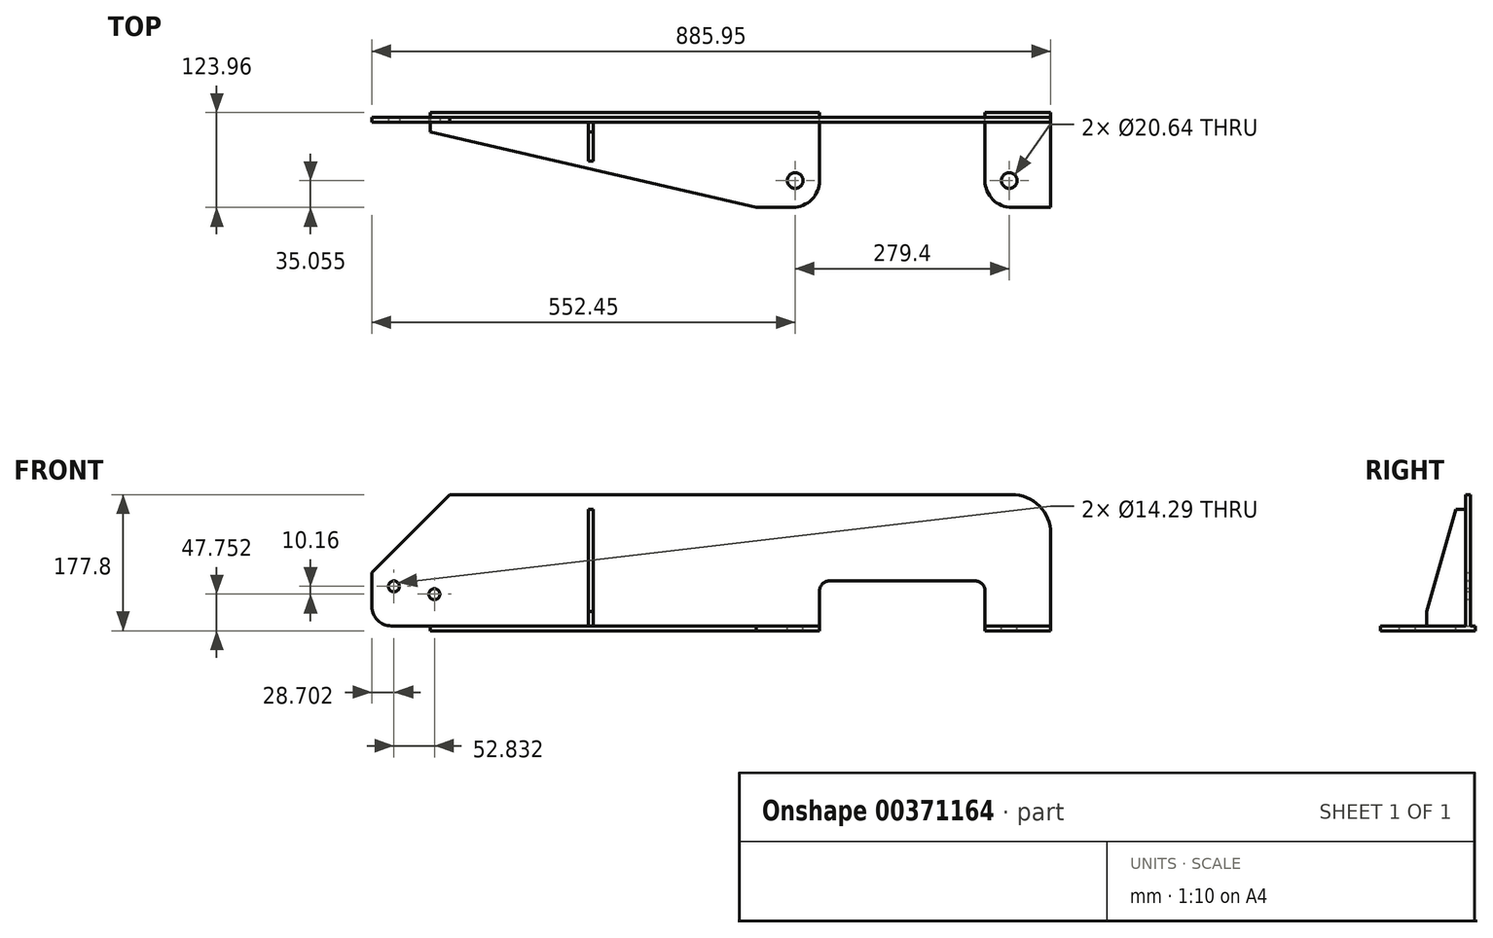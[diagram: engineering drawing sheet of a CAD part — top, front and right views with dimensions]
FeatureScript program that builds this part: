
annotation { "Feature Type Name" : "Feature", "Feature Type Description" : "" }
export const myFeature = defineFeature(function(context is Context, id is Id, definition is map)
    precondition{}
    {
        {
            var Q0;
            Q0=qCreatedBy(makeId("Front.planeOp"),FACE);
            var sketch = newSketch(context, id + "F0", { "sketchPlane" : qUnion([Q0])});
            skLineSegment(sketch, "E0", {"start": v(0, 99.97) * mm, "end": v(0, -95.52) * mm, "construction": true});
            skLineSegment(sketch, "E1.0", {"start": v(-107.95, 99.97) * mm, "end": v(-107.95, -95.52) * mm, "construction": true});
            skLineSegment(sketch, "E2.MirrorCS", {"start": v(107.95, 99.97) * mm, "end": v(107.95, -95.52) * mm, "construction": true});
            skLineSegment(sketch, "E3", {"start": v(-692.15, 0) * mm, "end": v(137.63, 0) * mm, "construction": true});
            skLineSegment(sketch, "E4.0", {"start": v(-198.58, 58.67) * mm, "end": v(137.63, 58.67) * mm, "construction": true});
            skLineSegment(sketch, "E5.0", {"start": v(-198.58, 171.45) * mm, "end": v(137.63, 171.45) * mm, "construction": true});
            skLineSegment(sketch, "E6.0", {"start": v(193.8, 171.45) * mm, "end": v(193.8, -95.52) * mm, "construction": true});
            skLineSegment(sketch, "E7.0", {"start": v(-692.15, 99.97) * mm, "end": v(-692.15, -95.52) * mm, "construction": true});
            skPoint(sketch, "E8.orphan", {"position": v(-198.58, 0) * mm});
            skLineSegment(sketch, "E9.bottom", {"start": v(-692.15, 0) * mm, "end": v(0, 0) * mm});
            skLineSegment(sketch, "E9.top", {"start": v(-692.15, 171.45) * mm, "end": v(143, 171.45) * mm});
            skLineSegment(sketch, "E9.left", {"start": v(-692.15, 0) * mm, "end": v(-692.15, 171.45) * mm});
            skLineSegment(sketch, "E9.right", {"start": v(193.8, 0) * mm, "end": v(193.8, 120.65) * mm});
            skLineSegment(sketch, "E10.bottom", {"start": v(-95.25, 58.67) * mm, "end": v(95.25, 58.67) * mm});
            skLineSegment(sketch, "E10.top", {"start": v(-107.95, 0) * mm, "end": v(0, 0) * mm});
            skLineSegment(sketch, "E10.left", {"start": v(-107.95, 45.97) * mm, "end": v(-107.95, 0) * mm});
            skLineSegment(sketch, "E10.right", {"start": v(107.95, 45.97) * mm, "end": v(107.95, 0) * mm});
            skLineSegment(sketch, "E11.trimOffspring", {"start": v(107.95, 0) * mm, "end": v(193.8, 0) * mm});
            skPoint(sketch, "E12.visualSharp", {"position": v(-107.95, 58.67) * mm});
            skArc(sketch, "E12.filletArc", {"start": v(-95.25, 58.67) * mm, "mid": v(-104.23, 54.95) * mm, "end": v(-107.95, 45.97) * mm});
            skPoint(sketch, "E13.visualSharp", {"position": v(107.95, 58.67) * mm});
            skArc(sketch, "E13.filletArc", {"start": v(107.95, 45.97) * mm, "mid": v(104.23, 54.95) * mm, "end": v(95.25, 58.67) * mm});
            skPoint(sketch, "E14.visualSharp", {"position": v(193.8, 171.45) * mm});
            skArc(sketch, "E14.filletArc", {"start": v(193.8, 120.65) * mm, "mid": v(178.92, 156.57) * mm, "end": v(143, 171.45) * mm});
            skSolve(sketch);
        }
        {
            var Q0;
            Q0 = qSketchRegion(id + "F0", true);
            extrude(context, id + "F1", {"entities" : qUnion([Q0]), "endBound" : BoundingType.SYMMETRIC, "depth" : 6.35 * mm});
        }
        {
            var Q0;
            Q0=makeQuery(id+"F1.opExtrude","SWEPT_EDGE",EDGE,{"disambiguationData":[OSD([sQuery(id+"F0.wireOp",EDGE,"E9.top"),sQuery(id+"F0.wireOp",EDGE,"E9.left")])]});
            chamfer(context, id + "F2", {"entities" : qUnion([Q0]), "width" : 101.6 * mm, "tangentPropagation" : true});
        }
        {
            var Q0;
            Q0=makeQuery(id+"F1.opExtrude","CAP_FACE",FACE,{"disambiguationData":[OSD([sQuery(id+"F0.wireOp",EDGE,"E9.bottom"),sQuery(id+"F0.wireOp",EDGE,"E9.top"),sQuery(id+"F0.wireOp",EDGE,"E9.left"),sQuery(id+"F0.wireOp",EDGE,"E9.right"),sQuery(id+"F0.wireOp",EDGE,"E10.bottom"),sQuery(id+"F0.wireOp",EDGE,"E10.left"),sQuery(id+"F0.wireOp",EDGE,"E10.right"),sQuery(id+"F0.wireOp",EDGE,"E11.trimOffspring"),sQuery(id+"F0.wireOp",EDGE,"E12.filletArc"),sQuery(id+"F0.wireOp",EDGE,"E13.filletArc"),sQuery(id+"F0.wireOp",EDGE,"E14.filletArc")])],"isStart":false});
            var sketch = newSketch(context, id + "F3", { "sketchPlane" : qUnion([Q0])});
            skLineSegment(sketch, "E15.0", {"start": v(-692.15, 0) * mm, "end": v(-692.15, 69.85) * mm, "construction": true});
            skLineSegment(sketch, "E16.0", {"start": v(-692.15, 0) * mm, "end": v(-107.95, 0) * mm, "construction": true});
            skLineSegment(sketch, "E17.0", {"start": v(-610.62, 0) * mm, "end": v(-610.62, 44.45) * mm, "construction": true});
            skLineSegment(sketch, "E18.0", {"start": v(-692.15, 41.4) * mm, "end": v(-107.95, 41.4) * mm, "construction": true});
            skPoint(sketch, "E19", {"position": v(-610.62, 41.4) * mm});
            skLineSegment(sketch, "E20.0", {"start": v(-663.45, 0) * mm, "end": v(-663.45, 51.56) * mm, "construction": true});
            skLineSegment(sketch, "E21.0", {"start": v(-692.15, 51.56) * mm, "end": v(-107.95, 51.56) * mm, "construction": true});
            skPoint(sketch, "E22", {"position": v(-663.45, 51.56) * mm});
            skSolve(sketch);
        }
        {
            var Q0;
            Q0=sQuery(id+"F3.wireOp",VERTEX,"E19");
            var Q1;
            Q1=sQuery(id+"F3.wireOp",VERTEX,"E22");
            var Q2;
            Q2=makeQuery(id+"F1.opExtrude","SWEPT_BODY",BODY,{"disambiguationData":[OSD([sQuery(id+"F0.wireOp",EDGE,"E9.bottom"),sQuery(id+"F0.wireOp",EDGE,"E9.top"),sQuery(id+"F0.wireOp",EDGE,"E9.left"),sQuery(id+"F0.wireOp",EDGE,"E9.right"),sQuery(id+"F0.wireOp",EDGE,"E10.bottom"),sQuery(id+"F0.wireOp",EDGE,"E10.left"),sQuery(id+"F0.wireOp",EDGE,"E10.right"),sQuery(id+"F0.wireOp",EDGE,"E11.trimOffspring"),sQuery(id+"F0.wireOp",EDGE,"E12.filletArc"),sQuery(id+"F0.wireOp",EDGE,"E13.filletArc"),sQuery(id+"F0.wireOp",EDGE,"E14.filletArc")])]});
            hole(context, id + "F4", {"style" : HoleStyle.SIMPLE, "endStyle" : HoleEndStyle.THROUGH, "holeDiameter" : 14.29 * mm, "isTappedThrough" : true, "tappedDepth" : 7.75 * mm, "tapClearance" : 3, "locations" : qUnion([Q0, Q1]), "scope" : qUnion([Q2])});
        }
        {
            var Q0;
            Q0=qCreatedBy(makeId("Top.planeOp"),FACE);
            var sketch = newSketch(context, id + "F5", { "sketchPlane" : qUnion([Q0])});
            skLineSegment(sketch, "E23.0", {"start": v(-615.94, 9.53) * mm, "end": v(193.8, 9.53) * mm});
            skLineSegment(sketch, "E24.0", {"start": v(-565.15, -114.43) * mm, "end": v(-143, -114.43) * mm});
            skLineSegment(sketch, "E25.0", {"start": v(193.8, -114.43) * mm, "end": v(193.8, 9.53) * mm});
            skPoint(sketch, "E26.orphan", {"position": v(193.8, 3.17) * mm});
            skLineSegment(sketch, "E27.0", {"start": v(107.95, -79.38) * mm, "end": v(107.95, 9.53) * mm});
            skLineSegment(sketch, "E28.0", {"start": v(-107.95, -79.38) * mm, "end": v(-107.95, 9.53) * mm});
            skPoint(sketch, "E29.orphan", {"position": v(193.8, -3.18) * mm});
            skLineSegment(sketch, "E30.trimOffspring", {"start": v(143, -114.43) * mm, "end": v(193.8, -114.43) * mm});
            skPoint(sketch, "E31.visualSharp", {"position": v(107.95, -114.43) * mm});
            skArc(sketch, "E31.filletArc", {"start": v(107.95, -79.38) * mm, "mid": v(118.22, -104.16) * mm, "end": v(143, -114.43) * mm});
            skPoint(sketch, "E32.visualSharp", {"position": v(-107.95, -114.43) * mm});
            skArc(sketch, "E32.filletArc", {"start": v(-143, -114.43) * mm, "mid": v(-118.22, -104.16) * mm, "end": v(-107.95, -79.38) * mm});
            skLineSegment(sketch, "E33", {"start": v(0, 141.84) * mm, "end": v(0, -163.46) * mm, "construction": true});
            skLineSegment(sketch, "E34.0", {"start": v(-139.7, 141.84) * mm, "end": v(-139.7, -163.46) * mm, "construction": true});
            skLineSegment(sketch, "E35.0", {"start": v(-190.5, 141.84) * mm, "end": v(-190.5, -163.46) * mm, "construction": true});
            skLineSegment(sketch, "E36.0", {"start": v(-615.94, 141.84) * mm, "end": v(-615.94, -163.46) * mm});
            skLineSegment(sketch, "E37.0", {"start": v(-615.94, -15.88) * mm, "end": v(-107.95, -15.88) * mm});
            skLineSegment(sketch, "E38", {"start": v(-190.5, -114.43) * mm, "end": v(-615.94, -15.88) * mm});
            skLineSegment(sketch, "E39.trimOffspring", {"start": v(0, -15.88) * mm, "end": v(193.8, -15.88) * mm});
            skSolve(sketch);
        }
        {
            var Q0;
            Q0 = qSketchRegion(id + "F5", true);
            extrude(context, id + "F6", {"entities" : qUnion([Q0]), "operationType" : NewBodyOperationType.ADD, "oppositeDirection" : true, "depth" : 6.35 * mm});
        }
        {
            var Q0;
            {var subQ0=sQuery(id+"F5.wireOp",EDGE,"E24.0");var subQ2=sQuery(id+"F5.wireOp",EDGE,"E28.0");var subQ4=sQuery(id+"F5.wireOp",EDGE,"E36.0");var subQ5=sQuery(id+"F5.wireOp",EDGE,"E32.filletArc");var subQ6=sQuery(id+"F5.wireOp",EDGE,"E38");Q0=makeQuery(id+"F6.boolean.opBoolean","SPLIT",FACE,{"disambiguationData":[TD([makeQuery(id+"F6.opExtrude","SWEPT_FACE",FACE,{"disambiguationData":[OSD([subQ0])]})])],"derivedFrom":makeQuery(id+"F6.opExtrude","CAP_FACE",FACE,{"disambiguationData":[OSD([sQuery(id+"F5.wireOp",EDGE,"E23.0"),subQ0,subQ2,subQ5,subQ4,subQ6])],"isStart":true})});}
            var sketch = newSketch(context, id + "F7", { "sketchPlane" : qUnion([Q0])});
            skLineSegment(sketch, "E40", {"start": v(0, 122.72) * mm, "end": v(0, -201.36) * mm, "construction": true});
            skLineSegment(sketch, "E41.0", {"start": v(-590.55, -3.18) * mm, "end": v(143, -3.18) * mm, "construction": true});
            skLineSegment(sketch, "E42.0", {"start": v(-565.15, -79.38) * mm, "end": v(143, -79.38) * mm, "construction": true});
            skLineSegment(sketch, "E43.0", {"start": v(-139.7, 122.72) * mm, "end": v(-139.7, -201.36) * mm, "construction": true});
            skPoint(sketch, "E44", {"position": v(-139.7, -79.38) * mm});
            skPoint(sketch, "E45.MirrorP", {"position": v(139.7, -79.38) * mm});
            skSolve(sketch);
        }
        {
            var Q0;
            Q0=sQuery(id+"F7.wireOp",VERTEX,"E44");
            var Q1;
            Q1=sQuery(id+"F7.wireOp",VERTEX,"E45.MirrorP");
            var Q2;
            Q2=makeQuery(id+"F1.opExtrude","SWEPT_BODY",BODY,{"disambiguationData":[OSD([sQuery(id+"F0.wireOp",EDGE,"E9.bottom"),sQuery(id+"F0.wireOp",EDGE,"E9.top"),sQuery(id+"F0.wireOp",EDGE,"E9.left"),sQuery(id+"F0.wireOp",EDGE,"E9.right"),sQuery(id+"F0.wireOp",EDGE,"E10.bottom"),sQuery(id+"F0.wireOp",EDGE,"E10.left"),sQuery(id+"F0.wireOp",EDGE,"E10.right"),sQuery(id+"F0.wireOp",EDGE,"E11.trimOffspring"),sQuery(id+"F0.wireOp",EDGE,"E12.filletArc"),sQuery(id+"F0.wireOp",EDGE,"E13.filletArc"),sQuery(id+"F0.wireOp",EDGE,"E14.filletArc")])]});
            hole(context, id + "F8", {"style" : HoleStyle.SIMPLE, "endStyle" : HoleEndStyle.THROUGH, "holeDiameter" : 20.64 * mm, "isTappedThrough" : true, "tappedDepth" : 7.75 * mm, "tapClearance" : 3, "locations" : qUnion([Q0, Q1]), "scope" : qUnion([Q2])});
        }
        {
            var Q0;
            Q0=qCreatedBy(makeId("Right.planeOp"),FACE);
            cPlane(context, id + "F9", {"entities" : qUnion([Q0]), "cplaneType" : CPlaneType.OFFSET, "offset" : 403.35 * mm, "oppositeDirection" : true, "width" : 152.4 * mm, "height" : 152.4 * mm});
        }
        {
            var Q0;
            Q0=qCreatedBy(id+"F9.planeOp",FACE);
            var sketch = newSketch(context, id + "F10", { "sketchPlane" : qUnion([Q0])});
            skLineSegment(sketch, "E46.0.0", {"start": v(-3.18, 0) * mm, "end": v(-3.18, 69.85) * mm, "construction": true});
            skLineSegment(sketch, "E46.0.1", {"start": v(-3.18, 69.85) * mm, "end": v(3.18, 69.85) * mm, "construction": true});
            skLineSegment(sketch, "E46.0.2", {"start": v(3.18, 69.85) * mm, "end": v(3.18, 0) * mm, "construction": true});
            skLineSegment(sketch, "E46.0.3", {"start": v(3.17, 0) * mm, "end": v(-3.18, 0) * mm, "construction": true});
            skLineSegment(sketch, "E47.0.0", {"start": v(3.18, 0) * mm, "end": v(9.53, 0) * mm, "construction": true});
            skLineSegment(sketch, "E47.0.1", {"start": v(9.53, 0) * mm, "end": v(9.53, -6.35) * mm, "construction": true});
            skLineSegment(sketch, "E47.0.2", {"start": v(9.53, -6.35) * mm, "end": v(-15.87, -6.35) * mm, "construction": true});
            skLineSegment(sketch, "E47.0.3", {"start": v(-15.87, -6.35) * mm, "end": v(-15.87, 0) * mm, "construction": true});
            skLineSegment(sketch, "E47.0.4", {"start": v(-15.87, 0) * mm, "end": v(-3.18, 0) * mm, "construction": true});
            skLineSegment(sketch, "E47.0.5", {"start": v(-3.18, 0) * mm, "end": v(3.18, 0) * mm, "construction": true});
            skLineSegment(sketch, "E48.bottom", {"start": v(-3.18, 0) * mm, "end": v(-53.97, 0) * mm});
            skLineSegment(sketch, "E48.top", {"start": v(-3.18, 152.4) * mm, "end": v(-15.88, 152.4) * mm});
            skLineSegment(sketch, "E48.left", {"start": v(-3.18, 0) * mm, "end": v(-3.18, 152.4) * mm});
            skLineSegment(sketch, "E48.right", {"start": v(-53.97, 0) * mm, "end": v(-53.97, 19.05) * mm});
            skLineSegment(sketch, "E49.0", {"start": v(-3.18, 19.05) * mm, "end": v(-53.97, 19.05) * mm, "construction": true});
            skLineSegment(sketch, "E50.0", {"start": v(-15.87, 0) * mm, "end": v(-15.88, 152.4) * mm, "construction": true});
            skLineSegment(sketch, "E51", {"start": v(-53.97, 19.05) * mm, "end": v(-15.88, 152.4) * mm});
            skSolve(sketch);
        }
        {
            var Q0;
            Q0 = qSketchRegion(id + "F10", true);
            extrude(context, id + "F11", {"entities" : qUnion([Q0]), "operationType" : NewBodyOperationType.ADD, "oppositeDirection" : true, "depth" : 6.35 * mm});
        }
        {
            var Q0;
            Q0=makeQuery(id+"F1.opExtrude","SWEPT_EDGE",EDGE,{"disambiguationData":[OSD([sQuery(id+"F0.wireOp",EDGE,"E9.bottom"),sQuery(id+"F0.wireOp",EDGE,"E9.left")])]});
            fillet(context, id + "F12", {"entities" : qUnion([Q0]), "radius" : 25.4 * mm, "tangentPropagation" : true, "allowEdgeOverflow" : false});
        }
    });
